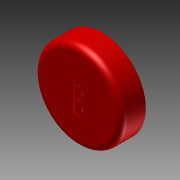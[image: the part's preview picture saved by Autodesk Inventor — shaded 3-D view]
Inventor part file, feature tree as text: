
AUTODESK INVENTOR PART (.ipt)
format: ipt  version: 2012 SP1 (Build 160190100, 190)  size: 131,584 bytes
history: native  units: in
note: dims shown in document units (in); Inventor stores cm internally (conversion verified against a paired STEP export)
features: extrude x2, sketch x2, fillet x1
ambient origin geometry x8: Origin, YZ Plane, XZ Plane, XY Plane, X Axis, Y Axis, Z Axis, Center Point
bodies: Solid1 (feature_tree)
feature tree (5):
  extrude  "Extrusion1"  Depth=0.1in TaperAngle=0.0deg
  fillet  "Fillet1"  Radius=0.025in
  extrude  "Extrusion2"  [1 undecoded]
  sketch  "Sketch1"  dims[d0=0.36in d1=0.1in d2=0.0in d3=0.025in]
  sketch  "Sketch2"  dims[d4=0.0025in d5=0.0in]
note: 1 required parameter value undecoded (feature->parameter linkage not recoverable at this tier; creation-order binding heuristic only, values carry confidence <= 0.55)
